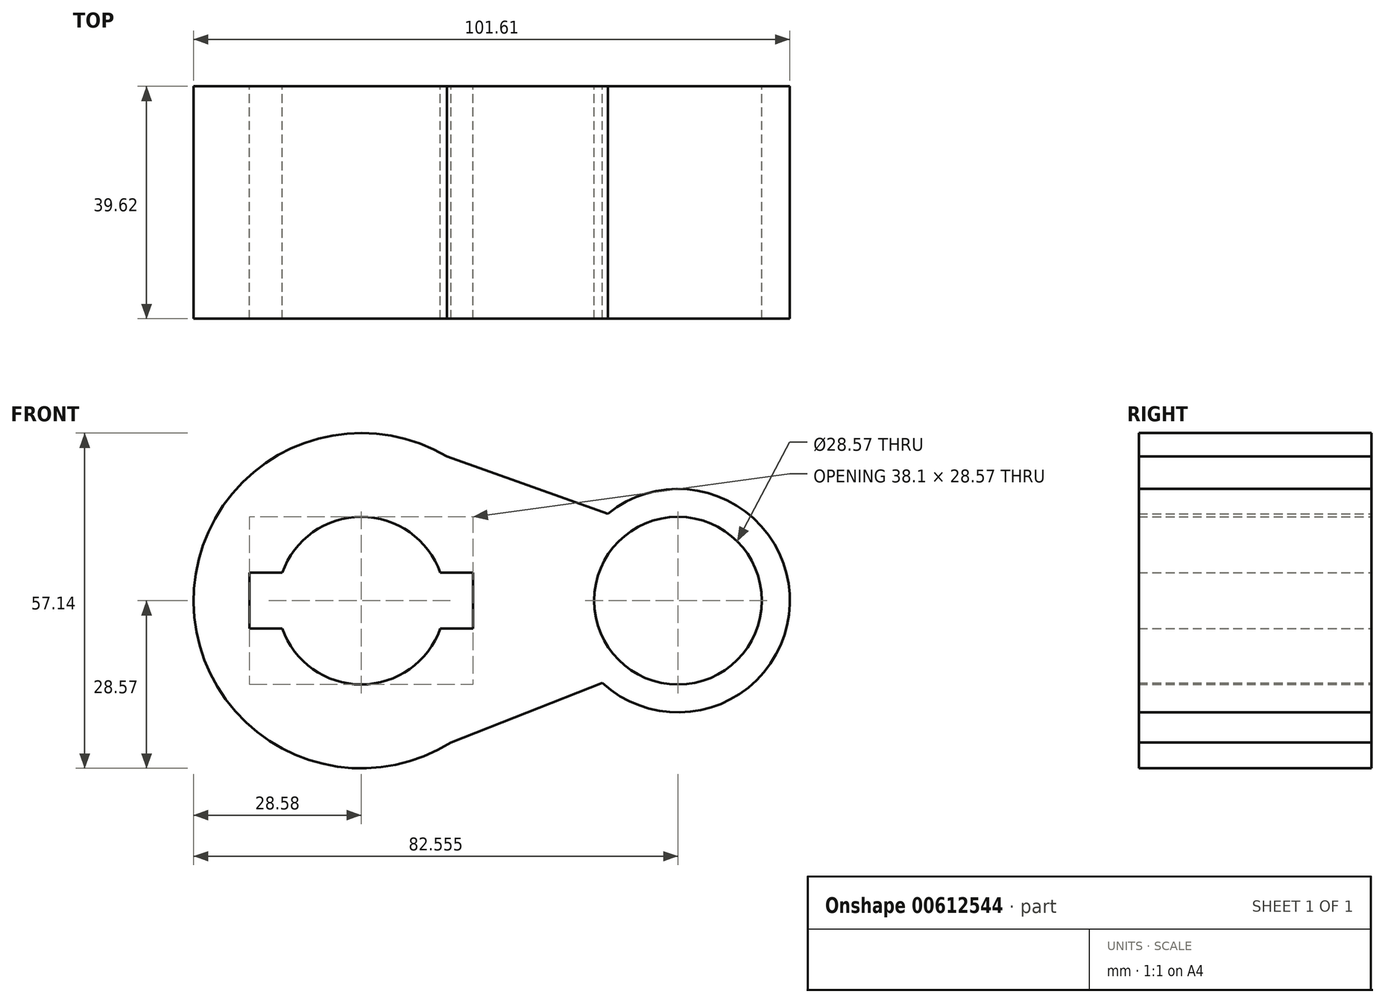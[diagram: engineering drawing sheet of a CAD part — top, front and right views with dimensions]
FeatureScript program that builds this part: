
annotation { "Feature Type Name" : "Feature", "Feature Type Description" : "" }
export const myFeature = defineFeature(function(context is Context, id is Id, definition is map)
    precondition{}
    {
        {
            var Q0;
            Q0=qCreatedBy(makeId("Front.planeOp"),FACE);
            var sketch = newSketch(context, id + "F0", { "sketchPlane" : qUnion([Q0])});
            skCircle(sketch, "E0", {"center": v(0, 0) * mm, "radius": 28.58 * mm});
            skCircle(sketch, "E1", {"center": v(53.98, 0) * mm, "radius": 19.05 * mm});
            skLineSegment(sketch, "E2", {"start": v(14.6, 24.56) * mm, "end": v(42.03, 14.84) * mm});
            skLineSegment(sketch, "E3", {"start": v(15.28, -24.15) * mm, "end": v(41.1, -14.04) * mm});
            skCircle(sketch, "E4", {"center": v(0, 0) * mm, "radius": 14.29 * mm});
            skCircle(sketch, "E5", {"center": v(53.98, 0) * mm, "radius": 14.29 * mm});
            skLineSegment(sketch, "E6.bottom", {"start": v(19.05, -4.76) * mm, "end": v(-19.05, -4.76) * mm});
            skLineSegment(sketch, "E6.top", {"start": v(19.05, 4.76) * mm, "end": v(-19.05, 4.76) * mm});
            skLineSegment(sketch, "E6.left", {"start": v(19.05, -4.76) * mm, "end": v(19.05, 4.76) * mm});
            skLineSegment(sketch, "E6.right", {"start": v(-19.05, -4.76) * mm, "end": v(-19.05, 4.76) * mm});
            skSolve(sketch);
        }
        {
            var Q0;
            Q0=makeQuery(id+"F0.imprint","IMPRINT",FACE,{"disambiguationData":[TD([[makeQuery(id+"F0.imprint","IMPRINT",EDGE,{"derivedFrom":sQuery(id+"F0.wireOp",EDGE,"E5")}),-1.0]])]});
            var Q1;
            {var subQ0=sQuery(id+"F0.wireOp",EDGE,"E2");Q1=makeQuery(id+"F0.imprint","IMPRINT",FACE,{"disambiguationData":[TD([[makeQuery(id+"F0.imprint","IMPRINT",EDGE,{"derivedFrom":subQ0}),-1.0]])]});}
            var Q2;
            {var subQ7=sQuery(id+"F0.wireOp",EDGE,"E6.left");Q2=makeQuery(id+"F0.imprint","IMPRINT",FACE,{"disambiguationData":[TD([[makeQuery(id+"F0.imprint","IMPRINT",EDGE,{"derivedFrom":subQ7}),-1.0]])]});}
            extrude(context, id + "F1", {"entities" : qUnion([Q0, Q1, Q2]), "depth" : 39.62 * mm, "offsetDistance" : 25.4 * mm});
        }
    });
